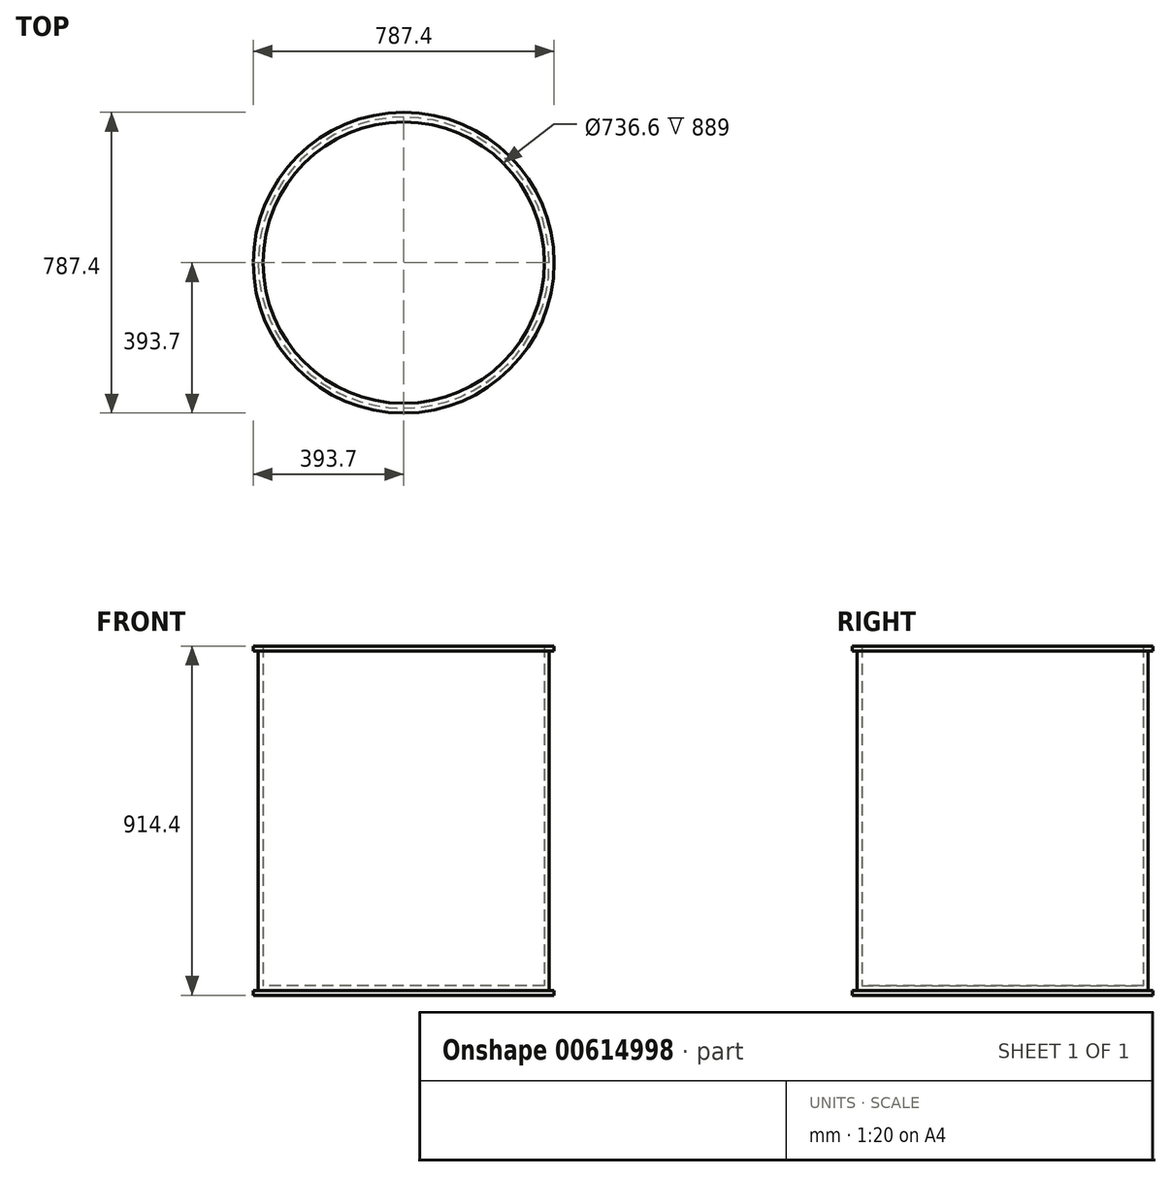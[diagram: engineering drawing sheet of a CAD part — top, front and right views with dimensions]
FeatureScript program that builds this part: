
annotation { "Feature Type Name" : "Feature", "Feature Type Description" : "" }
export const myFeature = defineFeature(function(context is Context, id is Id, definition is map)
    precondition{}
    {
        {
            var Q0;
            Q0=qCreatedBy(makeId("Top.planeOp"),FACE);
            var sketch = newSketch(context, id + "F0", { "sketchPlane" : qUnion([Q0])});
            skCircle(sketch, "E0", {"center": v(0, 0) * mm, "radius": 381 * mm});
            skCircle(sketch, "E1", {"center": v(0, 0) * mm, "radius": 368.3 * mm});
            skSolve(sketch);
        }
        {
            var Q0;
            Q0=makeQuery(id+"F0.imprint","IMPRINT",FACE,{"disambiguationData":[TD([[makeQuery(id+"F0.imprint","IMPRINT",EDGE,{"derivedFrom":sQuery(id+"F0.wireOp",EDGE,"E1")}),1.0]])]});
            extrude(context, id + "F1", {"entities" : qUnion([Q0]), "depth" : 25.4 * mm, "offsetDistance" : 25.4 * mm});
        }
        {
            var Q0;
            Q0 = qSketchRegion(id + "F0", true);
            extrude(context, id + "F2", {"entities" : qUnion([Q0]), "operationType" : NewBodyOperationType.ADD, "depth" : 914.4 * mm, "offsetDistance" : 25.4 * mm});
        }
        {
            var Q0;
            {var subQ0=sQuery(id+"F0.wireOp",EDGE,"E1");Q0=makeQuery(id+"F2.boolean.opBoolean","MERGE",FACE,{"derivedFrom":[makeQuery(id+"F1.opExtrude","CAP_FACE",FACE,{"disambiguationData":[OSD([subQ0])],"isStart":true}),makeQuery(id+"F2.opExtrude","CAP_FACE",FACE,{"disambiguationData":[OSD([sQuery(id+"F0.wireOp",EDGE,"E0"),subQ0])],"isStart":true})]});}
            var sketch = newSketch(context, id + "F3", { "sketchPlane" : qUnion([Q0])});
            skCircle(sketch, "E2", {"center": v(0, 0) * mm, "radius": 393.7 * mm});
            skSolve(sketch);
        }
        {
            var Q0;
            Q0=makeQuery(id+"F3.imprint","IMPRINT",FACE,{"disambiguationData":[TD([[makeQuery(id+"F3.imprint","IMPRINT",EDGE,{"derivedFrom":sQuery(id+"F3.wireOp",EDGE,"E2")}),1.0]])]});
            extrude(context, id + "F4", {"entities" : qUnion([Q0]), "operationType" : NewBodyOperationType.ADD, "oppositeDirection" : true, "depth" : 12.7 * mm, "offsetDistance" : 25.4 * mm});
        }
        {
            var Q0;
            Q0=makeQuery(id+"F2.opExtrude","CAP_FACE",FACE,{"disambiguationData":[OSD([sQuery(id+"F0.wireOp",EDGE,"E0"),sQuery(id+"F0.wireOp",EDGE,"E1")])],"isStart":false});
            var sketch = newSketch(context, id + "F5", { "sketchPlane" : qUnion([Q0])});
            skCircle(sketch, "E3", {"center": v(0, 0) * mm, "radius": 393.7 * mm});
            skCircle(sketch, "E4", {"center": v(0, 0) * mm, "radius": 368.3 * mm});
            skSolve(sketch);
        }
        {
            var Q0;
            Q0=makeQuery(id+"F5.imprint","IMPRINT",FACE,{"disambiguationData":[TD([[makeQuery(id+"F5.imprint","IMPRINT",EDGE,{"derivedFrom":sQuery(id+"F5.wireOp",EDGE,"E3")}),1.0]])]});
            extrude(context, id + "F6", {"entities" : qUnion([Q0]), "operationType" : NewBodyOperationType.ADD, "oppositeDirection" : true, "depth" : 12.7 * mm, "offsetDistance" : 25.4 * mm});
        }
    });
